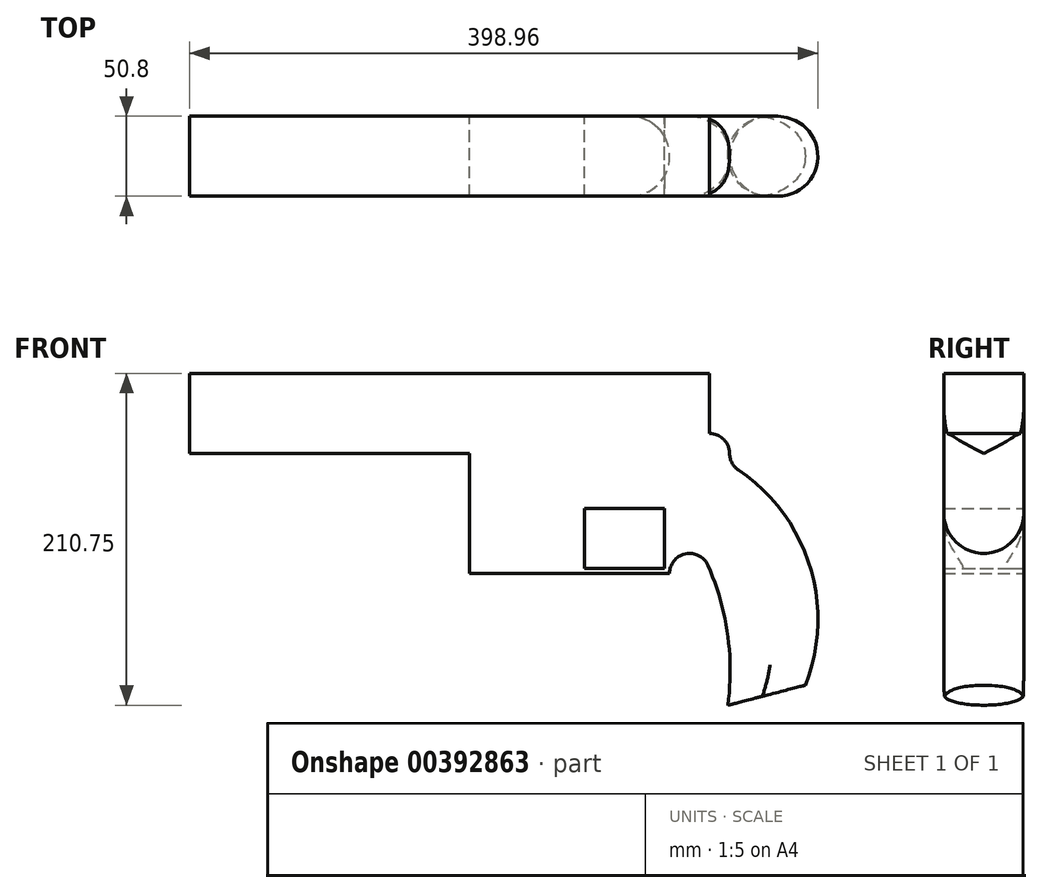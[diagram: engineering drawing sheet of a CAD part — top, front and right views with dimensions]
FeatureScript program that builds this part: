
annotation { "Feature Type Name" : "Feature", "Feature Type Description" : "" }
export const myFeature = defineFeature(function(context is Context, id is Id, definition is map)
    precondition{}
    {
        {
            var Q0;
            Q0=qCreatedBy(makeId("Front.planeOp"),FACE);
            var sketch = newSketch(context, id + "F0", { "sketchPlane" : qUnion([Q0])});
            skLineSegment(sketch, "E0", {"start": v(0, 0) * mm, "end": v(-177.8, 0) * mm});
            skLineSegment(sketch, "E1", {"start": v(-177.8, 0) * mm, "end": v(-177.8, 50.8) * mm});
            skLineSegment(sketch, "E2", {"start": v(-177.8, 50.8) * mm, "end": v(152.4, 50.8) * mm});
            skLineSegment(sketch, "E3", {"start": v(152.4, 50.8) * mm, "end": v(152.4, 12.7) * mm});
            skArc(sketch, "E4", {"start": v(213.2, -147.25) * mm, "mid": v(216, -71.42) * mm, "end": v(170.7, -10.53) * mm});
            skLineSegment(sketch, "E5", {"start": v(0, 0) * mm, "end": v(0, -76.2) * mm});
            skLineSegment(sketch, "E6", {"start": v(0, -76.2) * mm, "end": v(127, -76.2) * mm});
            skArc(sketch, "E7", {"start": v(151.31, -71.05) * mm, "mid": v(137.07, -63.78) * mm, "end": v(127, -76.2) * mm});
            skArc(sketch, "E8", {"start": v(164.01, -159.95) * mm, "mid": v(163.82, -114.62) * mm, "end": v(151.31, -71.05) * mm});
            skLineSegment(sketch, "E9", {"start": v(213.2, -147.25) * mm, "end": v(164.01, -159.95) * mm});
            skArc(sketch, "E10", {"start": v(165.1, 0) * mm, "mid": v(161.38, 8.98) * mm, "end": v(152.4, 12.7) * mm});
            skArc(sketch, "E11", {"start": v(165.1, 0) * mm, "mid": v(166.59, -5.97) * mm, "end": v(170.7, -10.53) * mm});
            skLineSegment(sketch, "E12.bottom", {"start": v(123.83, -73.03) * mm, "end": v(73.03, -73.03) * mm});
            skLineSegment(sketch, "E12.top", {"start": v(123.83, -34.93) * mm, "end": v(73.03, -34.93) * mm});
            skLineSegment(sketch, "E12.left", {"start": v(123.83, -73.03) * mm, "end": v(123.83, -34.92) * mm});
            skLineSegment(sketch, "E12.right", {"start": v(73.03, -73.03) * mm, "end": v(73.03, -34.92) * mm});
            skSolve(sketch);
        }
        {
            var Q0;
            Q0 = qSketchRegion(id + "F0", true);
            extrude(context, id + "F1", {"entities" : qUnion([Q0]), "depth" : 50.8 * mm});
        }
        {
            var Q0;
            Q0=makeQuery(id+"F1.opExtrude","CAP_EDGE",EDGE,{"disambiguationData":[OSD([sQuery(id+"F0.wireOp",EDGE,"E8")])],"isStart":false});
            var Q1;
            Q1=makeQuery(id+"F1.opExtrude","CAP_EDGE",EDGE,{"disambiguationData":[OSD([sQuery(id+"F0.wireOp",EDGE,"E8")])],"isStart":true});
            var Q2;
            Q2=makeQuery(id+"F1.opExtrude","CAP_EDGE",EDGE,{"disambiguationData":[OSD([sQuery(id+"F0.wireOp",EDGE,"E4")])],"isStart":false});
            var Q3;
            Q3=makeQuery(id+"F1.opExtrude","CAP_EDGE",EDGE,{"disambiguationData":[OSD([sQuery(id+"F0.wireOp",EDGE,"E4")])],"isStart":true});
            fillet(context, id + "F2", {"entities" : qUnion([Q0, Q1, Q2, Q3]), "radius" : 25.4 * mm, "tangentPropagation" : true, "allowEdgeOverflow" : false});
        }
    });
